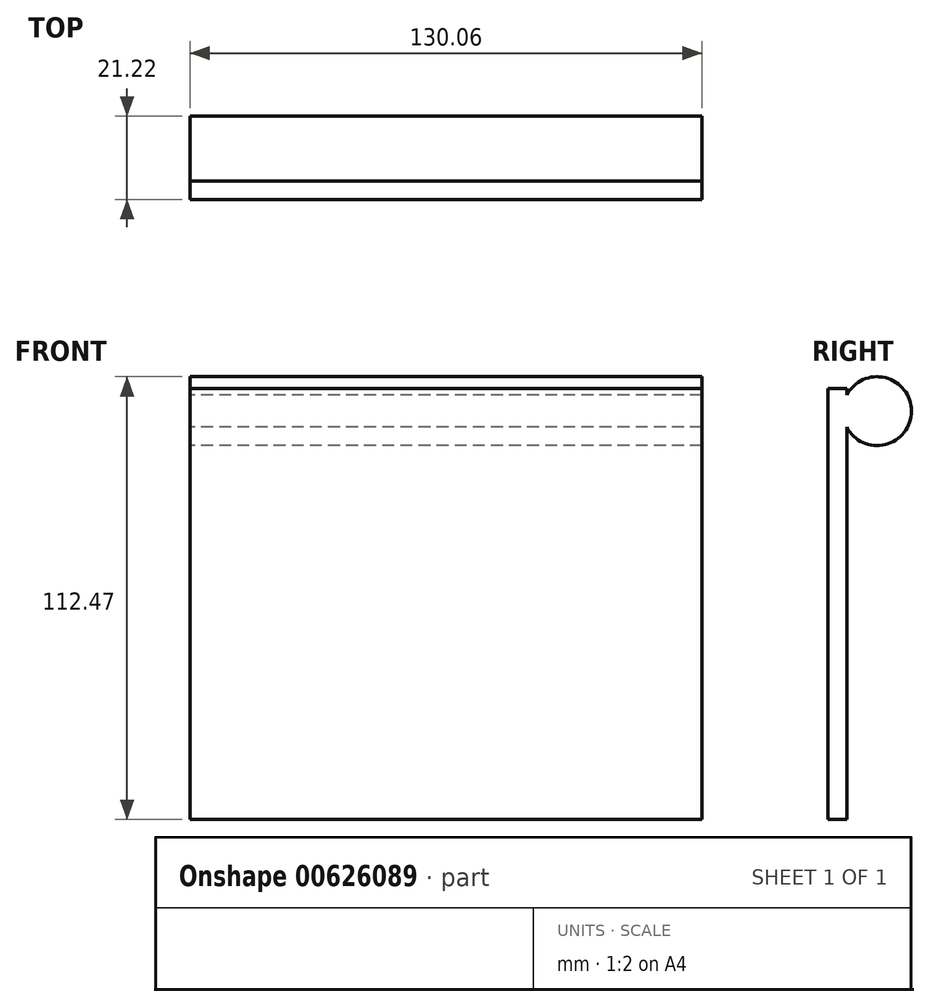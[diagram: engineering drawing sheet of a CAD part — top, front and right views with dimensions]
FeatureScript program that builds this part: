
annotation { "Feature Type Name" : "Feature", "Feature Type Description" : "" }
export const myFeature = defineFeature(function(context is Context, id is Id, definition is map)
    precondition{}
    {
        {
            var Q0;
            Q0=qCreatedBy(makeId("Front.planeOp"),FACE);
            var sketch = newSketch(context, id + "F0", { "sketchPlane" : qUnion([Q0])});
            skLineSegment(sketch, "E0.bottom", {"start": v(65.03, -54.73) * mm, "end": v(-65.03, -54.73) * mm});
            skLineSegment(sketch, "E0.top", {"start": v(65.03, 54.73) * mm, "end": v(-65.03, 54.73) * mm});
            skLineSegment(sketch, "E0.left", {"start": v(65.03, -54.73) * mm, "end": v(65.03, 54.73) * mm});
            skLineSegment(sketch, "E0.right", {"start": v(-65.03, -54.73) * mm, "end": v(-65.03, 54.73) * mm});
            skPoint(sketch, "E0.middle", {"position": v(0, 0) * mm});
            skSolve(sketch);
        }
        {
            var Q0;
            Q0 = qSketchRegion(id + "F0", true);
            extrude(context, id + "F1", {"entities" : qUnion([Q0]), "depth" : 4.77 * mm, "offsetDistance" : 25 * mm});
        }
        {
            var Q0;
            Q0=qCreatedBy(makeId("Right.planeOp"),FACE);
            var sketch = newSketch(context, id + "F2", { "sketchPlane" : qUnion([Q0])});
            skCircle(sketch, "E1", {"center": v(7.71, 49) * mm, "radius": 8.73 * mm});
            skSolve(sketch);
        }
        {
            var Q0;
            Q0=makeQuery(id+"F2.imprint","IMPRINT",FACE,{"disambiguationData":[TD([[makeQuery(id+"F2.imprint","IMPRINT",EDGE,{"derivedFrom":sQuery(id+"F2.wireOp",EDGE,"E1")}),1.0]])]});
            var Q1;
            Q1=makeQuery(id+"F1.opExtrude","SWEPT_FACE",FACE,{"disambiguationData":[OSD([sQuery(id+"F0.wireOp",EDGE,"E0.left")])]});
            var Q2;
            Q2=makeQuery(id+"F1.opExtrude","SWEPT_FACE",FACE,{"disambiguationData":[OSD([sQuery(id+"F0.wireOp",EDGE,"E0.right")])]});
            extrude(context, id + "F3", {"entities" : qUnion([Q0]), "operationType" : NewBodyOperationType.ADD, "endBound" : BoundingType.UP_TO_SURFACE, "depth" : 130.1 * mm, "endBoundEntityFace" : qUnion([Q1]), "offsetDistance" : 25 * mm, "hasSecondDirection" : true, "secondDirectionBound" : SecondDirectionBoundingType.UP_TO_SURFACE, "secondDirectionOppositeDirection" : true, "secondDirectionDepth" : 25 * mm, "secondDirectionBoundEntityFace" : qUnion([Q2])});
        }
    });
